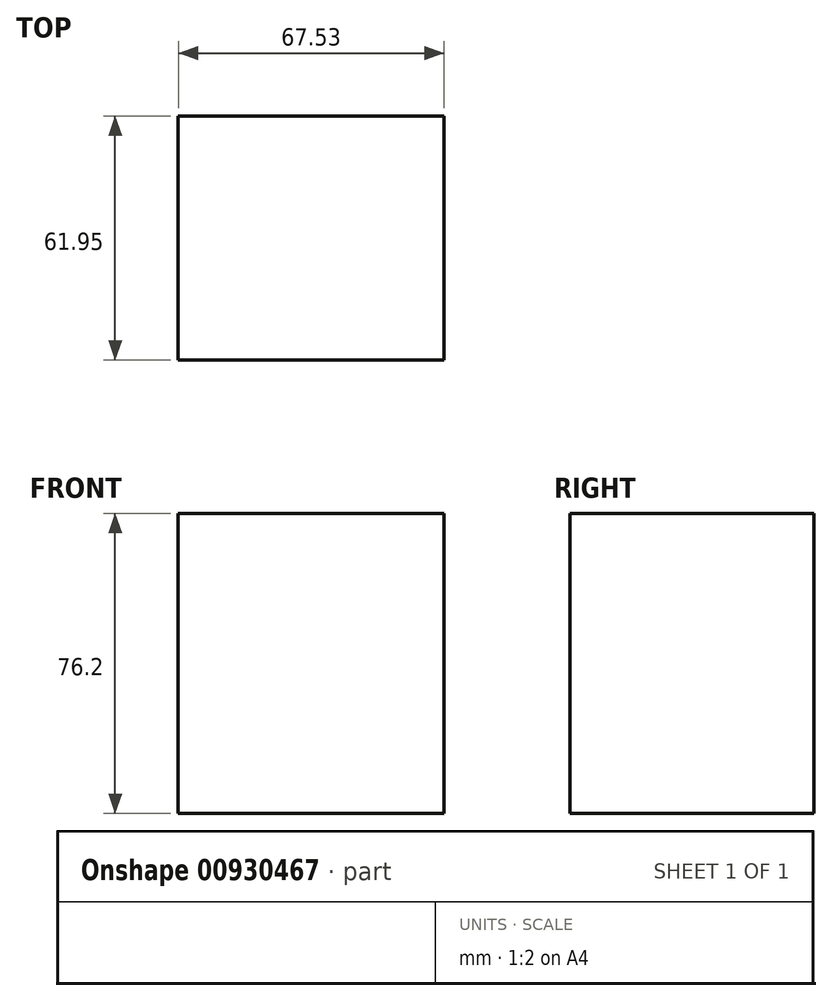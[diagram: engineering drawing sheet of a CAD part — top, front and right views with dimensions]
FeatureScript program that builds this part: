
annotation { "Feature Type Name" : "Feature", "Feature Type Description" : "" }
export const myFeature = defineFeature(function(context is Context, id is Id, definition is map)
    precondition{}
    {
        {
            var Q0;
            Q0=qCreatedBy(makeId("Top.planeOp"),FACE);
            var sketch = newSketch(context, id + "F0", { "sketchPlane" : qUnion([Q0])});
            skLineSegment(sketch, "E0.bottom", {"start": v(-49.47, 38.17) * mm, "end": v(18.06, 38.17) * mm});
            skLineSegment(sketch, "E0.top", {"start": v(-49.47, -23.78) * mm, "end": v(18.06, -23.78) * mm});
            skLineSegment(sketch, "E0.left", {"start": v(-49.47, 38.17) * mm, "end": v(-49.47, -23.78) * mm});
            skLineSegment(sketch, "E0.right", {"start": v(18.06, 38.17) * mm, "end": v(18.06, -23.78) * mm});
            skSolve(sketch);
        }
        {
            var Q0;
            Q0 = qSketchRegion(id + "F0", true);
            extrude(context, id + "F1", {"entities" : qUnion([Q0]), "depth" : 76.2 * mm, "offsetDistance" : 25.4 * mm});
        }
    });
